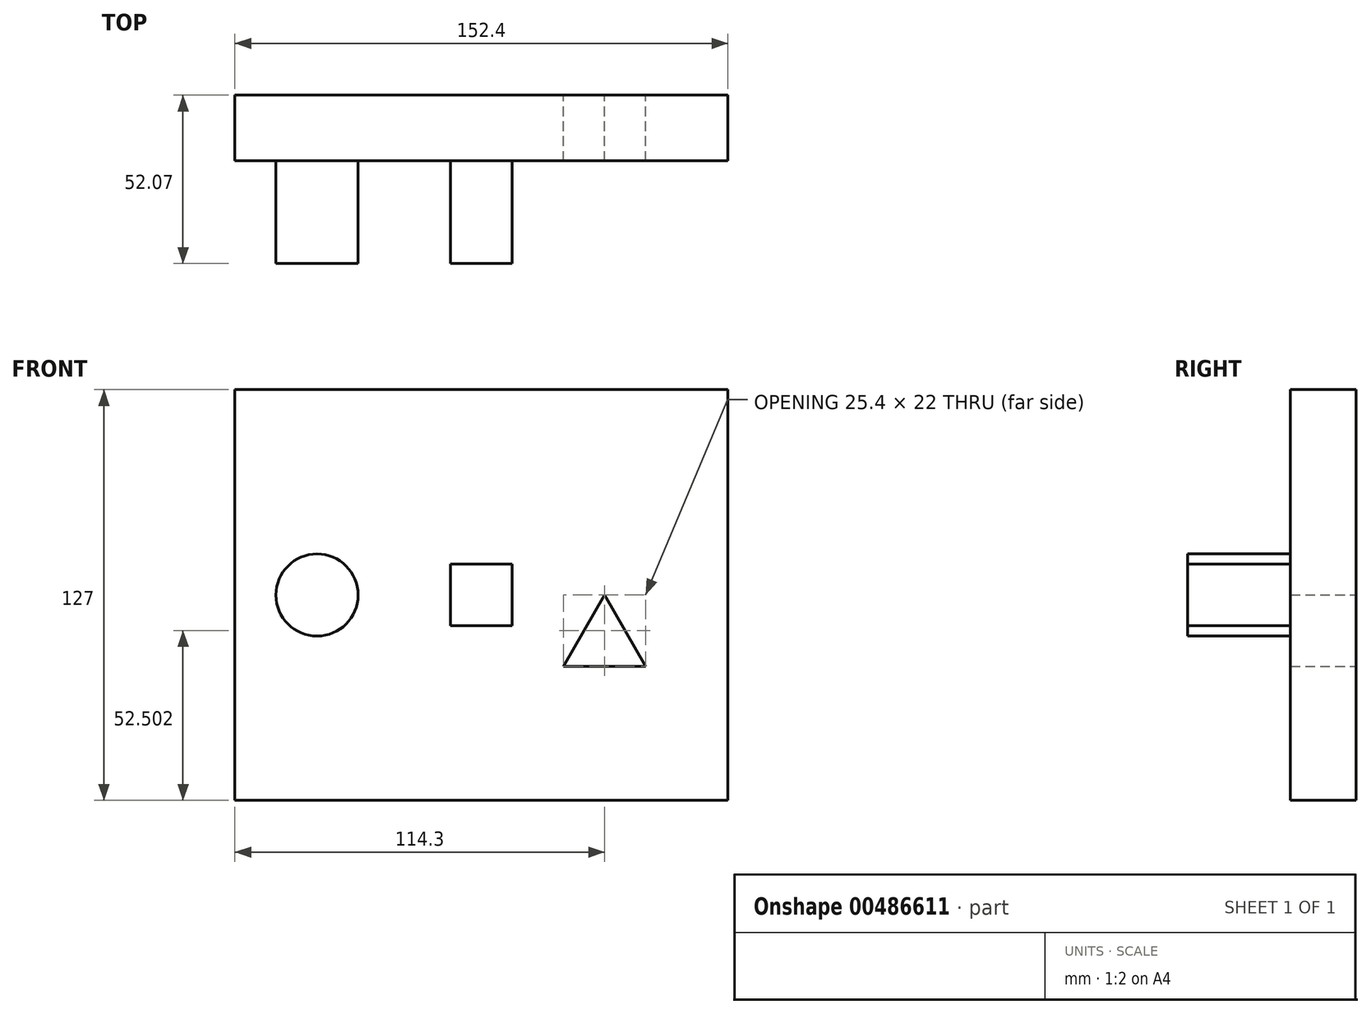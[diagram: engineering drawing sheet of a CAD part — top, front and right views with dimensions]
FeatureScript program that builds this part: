
annotation { "Feature Type Name" : "Feature", "Feature Type Description" : "" }
export const myFeature = defineFeature(function(context is Context, id is Id, definition is map)
    precondition{}
    {
        {
            var Q0;
            Q0=qCreatedBy(makeId("Front.planeOp"),FACE);
            var sketch = newSketch(context, id + "F0", { "sketchPlane" : qUnion([Q0])});
            skPoint(sketch, "E0.middle", {"position": v(0, 0) * mm});
            skLineSegment(sketch, "E1", {"start": v(0, 0) * mm, "end": v(6.35, 0) * mm});
            skLineSegment(sketch, "E2", {"start": v(6.35, 0) * mm, "end": v(-6.35, -22) * mm});
            skLineSegment(sketch, "E3", {"start": v(-6.35, -22) * mm, "end": v(19.05, -22) * mm});
            skLineSegment(sketch, "E4", {"start": v(19.05, -22) * mm, "end": v(6.35, 0) * mm});
            skLineSegment(sketch, "E5", {"start": v(0, 0) * mm, "end": v(-31.75, 0) * mm});
            skLineSegment(sketch, "E6.bottom", {"start": v(-22.22, 9.53) * mm, "end": v(-41.28, 9.53) * mm});
            skLineSegment(sketch, "E6.top", {"start": v(-22.22, -9.53) * mm, "end": v(-41.28, -9.52) * mm});
            skLineSegment(sketch, "E6.left", {"start": v(-22.22, 9.53) * mm, "end": v(-22.22, -9.53) * mm});
            skLineSegment(sketch, "E6.right", {"start": v(-41.27, 9.53) * mm, "end": v(-41.27, -9.52) * mm});
            skPoint(sketch, "E6.middle", {"position": v(-31.75, 0) * mm});
            skLineSegment(sketch, "E7", {"start": v(-31.75, 0) * mm, "end": v(-82.55, 0) * mm});
            skPoint(sketch, "E7.endSnap0", {"position": v(-76.2, 0) * mm});
            skCircle(sketch, "E8", {"center": v(-82.55, 0) * mm, "radius": 12.7 * mm});
            skLineSegment(sketch, "E9.bottom", {"start": v(44.45, 63.5) * mm, "end": v(-107.95, 63.5) * mm});
            skLineSegment(sketch, "E9.top", {"start": v(44.45, -63.5) * mm, "end": v(-107.95, -63.5) * mm});
            skLineSegment(sketch, "E9.left", {"start": v(44.45, 63.5) * mm, "end": v(44.45, -63.5) * mm});
            skLineSegment(sketch, "E9.right", {"start": v(-107.95, 63.5) * mm, "end": v(-107.95, -63.5) * mm});
            skSolve(sketch);
        }
        {
            var Q0;
            Q0=makeQuery(id+"F0.imprint","IMPRINT",FACE,{"disambiguationData":[TD([[makeQuery(id+"F0.imprint","IMPRINT",EDGE,{"derivedFrom":sQuery(id+"F0.wireOp",EDGE,"E2")}),-1.0]])]});
            extrude(context, id + "F1", {"entities" : qUnion([Q0]), "depth" : 20.32 * mm});
        }
        {
            var Q0;
            Q0=makeQuery(id+"F0.imprint","IMPRINT",FACE,{"disambiguationData":[TD([[makeQuery(id+"F0.imprint","IMPRINT",EDGE,{"derivedFrom":sQuery(id+"F0.wireOp",EDGE,"E8")}),1.0]])]});
            extrude(context, id + "F2", {"entities" : qUnion([Q0]), "operationType" : NewBodyOperationType.ADD, "depth" : 52.07 * mm});
        }
        {
            var Q0;
            {var subQ1=sQuery(id+"F0.wireOp",EDGE,"E6.top");Q0=makeQuery(id+"F0.imprint","IMPRINT",FACE,{"disambiguationData":[TD([[makeQuery(id+"F0.imprint","IMPRINT",EDGE,{"derivedFrom":subQ1}),-1.0]])]});}
            var Q1;
            {var subQ1=sQuery(id+"F0.wireOp",EDGE,"E6.bottom");Q1=makeQuery(id+"F0.imprint","IMPRINT",FACE,{"disambiguationData":[TD([[makeQuery(id+"F0.imprint","IMPRINT",EDGE,{"derivedFrom":subQ1}),1.0]])]});}
            extrude(context, id + "F3", {"entities" : qUnion([Q0, Q1]), "operationType" : NewBodyOperationType.ADD, "depth" : 52.07 * mm});
        }
    });
